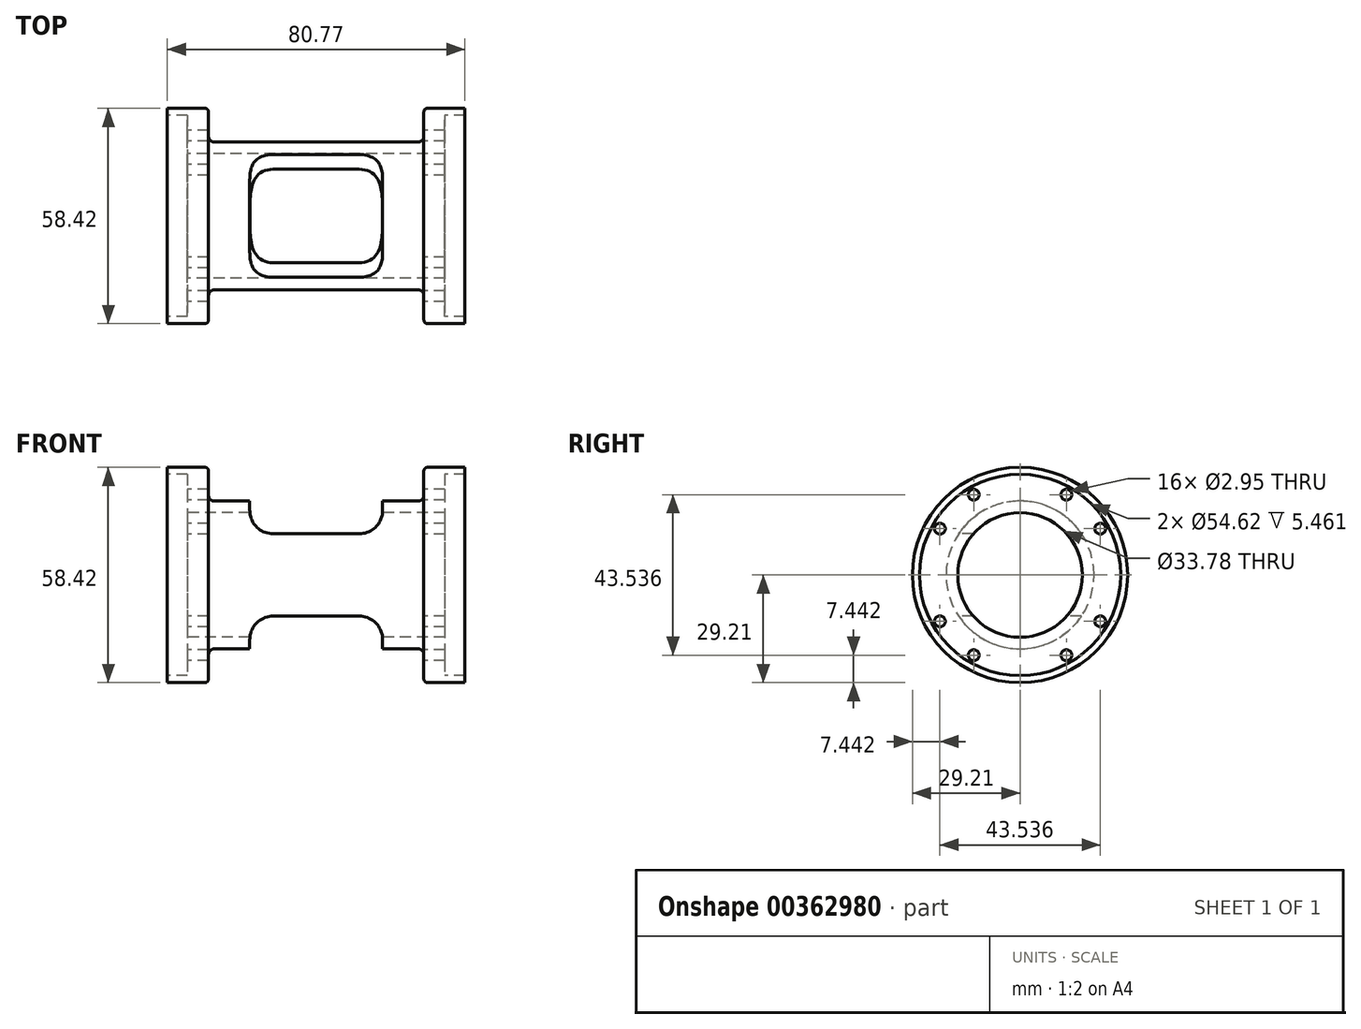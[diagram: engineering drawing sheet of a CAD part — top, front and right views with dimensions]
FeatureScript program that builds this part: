
annotation { "Feature Type Name" : "Feature", "Feature Type Description" : "" }
export const myFeature = defineFeature(function(context is Context, id is Id, definition is map)
    precondition{}
    {
        {
            var Q0;
            Q0=qCreatedBy(makeId("Front.planeOp"),FACE);
            var sketch = newSketch(context, id + "F0", { "sketchPlane" : qUnion([Q0])});
            skLineSegment(sketch, "E0", {"start": v(-130.15, 0) * mm, "end": v(120.43, 0) * mm, "construction": true});
            skLineSegment(sketch, "E1", {"start": v(-116.34, -27.31) * mm, "end": v(-110.88, -27.31) * mm});
            skLineSegment(sketch, "E2", {"start": v(-110.88, -27.31) * mm, "end": v(-110.88, -16.9) * mm});
            skLineSegment(sketch, "E3", {"start": v(-110.88, -16.9) * mm, "end": v(-41.03, -16.9) * mm});
            skLineSegment(sketch, "E4", {"start": v(-41.03, -16.9) * mm, "end": v(-41.03, -27.31) * mm});
            skLineSegment(sketch, "E5", {"start": v(-41.03, -27.31) * mm, "end": v(-35.57, -27.31) * mm});
            skLineSegment(sketch, "E6", {"start": v(-116.34, -29.21) * mm, "end": v(-106.18, -29.21) * mm});
            skLineSegment(sketch, "E7", {"start": v(-35.57, -27.31) * mm, "end": v(-35.57, -29.21) * mm});
            skLineSegment(sketch, "E8", {"start": v(-116.34, -27.31) * mm, "end": v(-116.34, -29.21) * mm});
            skPoint(sketch, "E9.startSnap0", {"position": v(-110.88, -22.1) * mm});
            skLineSegment(sketch, "E10", {"start": v(-103.64, -20.07) * mm, "end": v(-48.27, -20.07) * mm});
            skLineSegment(sketch, "E11.0", {"start": v(-46.75, -21.6) * mm, "end": v(-46.75, -28.2) * mm});
            skLineSegment(sketch, "E12.0", {"start": v(-105.17, -21.6) * mm, "end": v(-105.17, -28.2) * mm});
            skLineSegment(sketch, "E13.trimOffspring", {"start": v(-45.73, -29.21) * mm, "end": v(-35.57, -29.21) * mm});
            skPoint(sketch, "E14.visualSharp", {"position": v(-105.17, -20.07) * mm});
            skArc(sketch, "E14.filletArc", {"start": v(-103.64, -20.07) * mm, "mid": v(-104.72, -20.51) * mm, "end": v(-105.17, -21.6) * mm});
            skPoint(sketch, "E15.visualSharp", {"position": v(-46.75, -20.07) * mm});
            skArc(sketch, "E15.filletArc", {"start": v(-46.75, -21.6) * mm, "mid": v(-47.2, -20.51) * mm, "end": v(-48.27, -20.07) * mm});
            skPoint(sketch, "E16.visualSharp", {"position": v(-105.17, -29.21) * mm});
            skArc(sketch, "E16.filletArc", {"start": v(-106.18, -29.21) * mm, "mid": v(-105.47, -28.91) * mm, "end": v(-105.17, -28.2) * mm});
            skPoint(sketch, "E17.visualSharp", {"position": v(-46.75, -29.21) * mm});
            skArc(sketch, "E17.filletArc", {"start": v(-46.75, -28.2) * mm, "mid": v(-46.45, -28.91) * mm, "end": v(-45.73, -29.2) * mm});
            skSolve(sketch);
        }
        {
            var Q0;
            Q0=makeQuery(id+"F0.imprint","IMPRINT",FACE,{"disambiguationData":[TD([[makeQuery(id+"F0.imprint","IMPRINT",EDGE,{"derivedFrom":sQuery(id+"F0.wireOp",EDGE,"E1")}),-1.0]])]});
            var Q1;
            Q1=sQuery(id+"F0.wireOp",EDGE,"E0");
            revolve(context, id + "F1", {"entities" : qUnion([Q0]), "axis" : qUnion([Q1]), "revolveType" : RevolveType.FULL});
        }
        {
            var Q0;
            Q0=qCreatedBy(makeId("Front.planeOp"),FACE);
            var sketch = newSketch(context, id + "F2", { "sketchPlane" : qUnion([Q0])});
            skLineSegment(sketch, "E18.0", {"start": v(-46.75, -28.2) * mm, "end": v(-46.75, 28.2) * mm});
            skLineSegment(sketch, "E19", {"start": v(-103.64, 20.07) * mm, "end": v(-48.27, 20.07) * mm});
            skLineSegment(sketch, "E20.0", {"start": v(-35.57, -29.21) * mm, "end": v(-35.57, 29.21) * mm});
            skLineSegment(sketch, "E21", {"start": v(-35.57, 0) * mm, "end": v(-124.06, 0) * mm});
            skPoint(sketch, "E21.endSnap0", {"position": v(-35.57, 0) * mm});
            skLineSegment(sketch, "E22.0", {"start": v(-35.57, 11.18) * mm, "end": v(-46.75, 11.18) * mm});
            skLineSegment(sketch, "E23.0", {"start": v(-35.57, -11.18) * mm, "end": v(-46.75, -11.18) * mm});
            skLineSegment(sketch, "E24.0", {"start": v(-57.92, -28.2) * mm, "end": v(-57.92, -17.53) * mm});
            skLineSegment(sketch, "E25", {"start": v(-105.17, -28.2) * mm, "end": v(-105.17, 28.2) * mm});
            skLineSegment(sketch, "E26.0", {"start": v(-94, -28.2) * mm, "end": v(-94, -17.53) * mm});
            skLineSegment(sketch, "E27.trimOffspring", {"start": v(-94, 17.53) * mm, "end": v(-94, 28.2) * mm});
            skLineSegment(sketch, "E28.trimOffspring", {"start": v(-57.92, 17.53) * mm, "end": v(-57.92, 28.2) * mm});
            skLineSegment(sketch, "E29.trimOffspring", {"start": v(-105.17, -11.18) * mm, "end": v(-124.06, -11.18) * mm});
            skLineSegment(sketch, "E30.trimOffspring", {"start": v(-105.17, 11.18) * mm, "end": v(-124.06, 11.18) * mm});
            skLineSegment(sketch, "E31.trimOffspring", {"start": v(-64.27, 11.18) * mm, "end": v(-87.64, 11.18) * mm});
            skLineSegment(sketch, "E32.trimOffspring", {"start": v(-64.27, -11.18) * mm, "end": v(-87.64, -11.18) * mm});
            skPoint(sketch, "E33.visualSharp", {"position": v(-94, 11.18) * mm});
            skArc(sketch, "E33.filletArc", {"start": v(-94, 17.53) * mm, "mid": v(-92.13, 13.04) * mm, "end": v(-87.64, 11.18) * mm});
            skPoint(sketch, "E34.visualSharp", {"position": v(-57.92, 11.18) * mm});
            skArc(sketch, "E34.filletArc", {"start": v(-64.27, 11.18) * mm, "mid": v(-59.78, 13.04) * mm, "end": v(-57.92, 17.53) * mm});
            skPoint(sketch, "E35.visualSharp", {"position": v(-57.92, -11.18) * mm});
            skArc(sketch, "E35.filletArc", {"start": v(-57.92, -17.53) * mm, "mid": v(-59.78, -13.04) * mm, "end": v(-64.27, -11.18) * mm});
            skPoint(sketch, "E36.visualSharp", {"position": v(-94, -11.18) * mm});
            skArc(sketch, "E36.filletArc", {"start": v(-87.64, -11.18) * mm, "mid": v(-92.13, -13.04) * mm, "end": v(-94, -17.53) * mm});
            skLineSegment(sketch, "E37", {"start": v(-48.27, -20.07) * mm, "end": v(-103.64, -20.07) * mm});
            skSolve(sketch);
        }
        {
            var Q0;
            Q0=makeQuery(id+"F2.imprint","IMPRINT",FACE,{"disambiguationData":[TD([[makeQuery(id+"F2.imprint","IMPRINT",EDGE,{"derivedFrom":sQuery(id+"F2.wireOp",EDGE,"E31.trimOffspring")}),-1.0]])]});
            var Q1;
            Q1=makeQuery(id+"F2.imprint","IMPRINT",FACE,{"disambiguationData":[TD([[makeQuery(id+"F2.imprint","IMPRINT",EDGE,{"derivedFrom":sQuery(id+"F2.wireOp",EDGE,"E32.trimOffspring")}),1.0]])]});
            extrude(context, id + "F3", {"entities" : qUnion([Q0, Q1]), "operationType" : NewBodyOperationType.REMOVE, "endBound" : BoundingType.SYMMETRIC, "oppositeDirection" : true, "depth" : 43.69 * mm});
        }
        {
            var Q0;
            Q0=makeQuery(id+"F1.opRevolve","SWEPT_FACE",FACE,{"disambiguationData":[OSD([sQuery(id+"F0.wireOp",EDGE,"E2")])]});
            var sketch = newSketch(context, id + "F4", { "sketchPlane" : qUnion([Q0])});
            skPoint(sketch, "E38", {"position": v(12.57, 21.77) * mm});
            skPoint(sketch, "E39", {"position": v(21.77, 12.57) * mm});
            skPoint(sketch, "E40.1.0", {"position": v(-12.57, 21.77) * mm});
            skPoint(sketch, "E40.1.1", {"position": v(-21.77, 12.57) * mm});
            skPoint(sketch, "E40.2.0", {"position": v(-21.77, -12.57) * mm});
            skPoint(sketch, "E40.2.1", {"position": v(-12.57, -21.77) * mm});
            skPoint(sketch, "E40.3.0", {"position": v(12.57, -21.77) * mm});
            skPoint(sketch, "E40.3.1", {"position": v(21.77, -12.57) * mm});
            skPoint(sketch, "E40.center", {"position": v(0, 0) * mm});
            skSolve(sketch);
        }
        {
            var Q0;
            Q0=sQuery(id+"F4.wireOp",VERTEX,"E38");
            var Q1;
            Q1=sQuery(id+"F4.wireOp",VERTEX,"E39");
            var Q2;
            Q2=sQuery(id+"F4.wireOp",VERTEX,"E40.3.1");
            var Q3;
            Q3=sQuery(id+"F4.wireOp",VERTEX,"E40.3.0");
            var Q4;
            Q4=sQuery(id+"F4.wireOp",VERTEX,"E40.2.1");
            var Q5;
            Q5=sQuery(id+"F4.wireOp",VERTEX,"E40.2.0");
            var Q6;
            Q6=sQuery(id+"F4.wireOp",VERTEX,"E40.1.1");
            var Q7;
            Q7=sQuery(id+"F4.wireOp",VERTEX,"E40.1.0");
            var Q8;
            Q8=makeQuery(id+"F1.opRevolve","SWEPT_BODY",BODY,{"disambiguationData":[OSD([sQuery(id+"F0.wireOp",EDGE,"E1"),sQuery(id+"F0.wireOp",EDGE,"E2"),sQuery(id+"F0.wireOp",EDGE,"E3"),sQuery(id+"F0.wireOp",EDGE,"E4"),sQuery(id+"F0.wireOp",EDGE,"E5"),sQuery(id+"F0.wireOp",EDGE,"E6"),sQuery(id+"F0.wireOp",EDGE,"E7"),sQuery(id+"F0.wireOp",EDGE,"E8"),sQuery(id+"F0.wireOp",EDGE,"E10"),sQuery(id+"F0.wireOp",EDGE,"E11.0"),sQuery(id+"F0.wireOp",EDGE,"E12.0"),sQuery(id+"F0.wireOp",EDGE,"E13.trimOffspring"),sQuery(id+"F0.wireOp",EDGE,"E14.filletArc"),sQuery(id+"F0.wireOp",EDGE,"E15.filletArc"),sQuery(id+"F0.wireOp",EDGE,"E16.filletArc"),sQuery(id+"F0.wireOp",EDGE,"E17.filletArc")])]});
            hole(context, id + "F5", {"style" : HoleStyle.SIMPLE, "endStyle" : HoleEndStyle.THROUGH, "standardTappedOrClearance" : lookupTablePath({ "standard" : "ANSI", "size" : "#32 (0.12)", "type" : "Drilled" }), "standardBlindInLast" : lookupTablePath({ "standard" : "ANSI", "size" : "#32", "type" : "Drilled" }), "holeDiameter" : 2.95 * mm, "tappedDepth" : 5.4 * mm, "tapClearance" : 3, "locations" : qUnion([Q0, Q1, Q2, Q3, Q4, Q5, Q6, Q7]), "scope" : qUnion([Q8])});
        }
    });
